# Revit family: Construction_Stairs-Precision_Ladders-Roof_Hatch-V1
name_source: partatom
category: Specialty Equipment
units: mm (PartAtom-declared; Revit-internal decimal feet)

## family parameters
Cut with Voids When Loaded = Yes
Host = Face
OmniClass Number = 23.30.10.27.24
OmniClass Title = Roof Hatches
Part Type = Normal
Room Calculation Point = No
Round Connector Dimension = Use Diameter
Shared = No

## types (10) — shared parameters
Clear Opening Length MAX = 96"
Clear Opening Length MIN = 36"
Clear Opening Width = 30"
Clear Opening Width MAX = 48"
Clear Opening Width MIN = 30"
Default Elevation = 0"
Description = Roof Hatch
Insulation Material = Insulation -Precision Ladders LLC - Rigid Fiber
Manufacturer = Precision Ladders, LLC
Model = Roof Hatches
Opening Width Real = 30"
Product Page URL = http://www.precisionladders.com
Product data url = https://www.bimobject.com
URL = http://www.precisionladders.com

## per-type parameters (varying)
| type | Clear Opening Length | Handle on Long Side | Handle on Short Side | Material | Opening Length Real |
| PH-(A) 2’-6” X 3’-0” | 36" | No | Yes | Metal - Precision Ladders LLC - Aluminum - Mill Finish | 36" |
| PH-(A) 2’-6” X 4’-6” | 54" | Yes | No | Metal - Precision Ladders LLC - Aluminum - Mill Finish | 54" |
| PH-(A) 2’-6” X 5’-4” | 64" | Yes | No | Metal - Precision Ladders LLC - Aluminum - Mill Finish | 64" |
| PH-(A) 2’-6” X 6’-0” | 72" | Yes | No | Metal - Precision Ladders LLC - Aluminum - Mill Finish | 72" |
| PH-(G) 2’-6” X 6’-0” | 72" | Yes | No | Metal - Precision Ladders LLC - Steel - Galvanized red oxide | 72" |
| PH-(G) 2’-6” X 5’-4” | 64" | Yes | No | Metal - Precision Ladders LLC - Steel - Galvanized red oxide | 64" |
| PH-(G) 2’-6” X 4’-6” | 54" | Yes | No | Metal - Precision Ladders LLC - Steel - Galvanized red oxide | 54" |
| PH-(A) Custom Size | 96" | Yes | No | Metal - Precision Ladders LLC - Aluminum - Mill Finish | 96" |
| PH-(G) Custom Size | 96" | Yes | No | Metal - Precision Ladders LLC - Steel - Galvanized red oxide | 96" |
| PH-(G) 2’-6” X 3’-0” | 36" | No | Yes | Metal - Precision Ladders LLC - Steel - Galvanized red oxide | 36" |

note: column(s) folded — value = type name in every type: Model Number

## geometry (parser evidence)
native form markers: Sweep x2
no freeform markers — native parametric forms only
